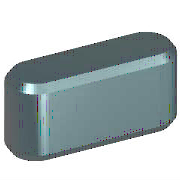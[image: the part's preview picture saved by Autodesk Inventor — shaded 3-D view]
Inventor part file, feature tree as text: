
AUTODESK INVENTOR PART (.ipt)
format: ipt  version: 2025 (Build 290162000, 162)  size: 139,264 bytes
history: native  units: mm (DEFAULTED — no unit token found)
features: plane x3, extrude x1
ambient origin geometry x8: Origin, YZ Plane, XZ Plane, XY Plane, X Axis, Y Axis, Z Axis, Center Point
bodies: Solid1 (feature_tree)
feature tree (4):
  plane  "Work Plane1"
  plane  "Work Plane2"
  extrude  "轴承体1"  Depth=7.0mm
  plane  "Work Plane3"
